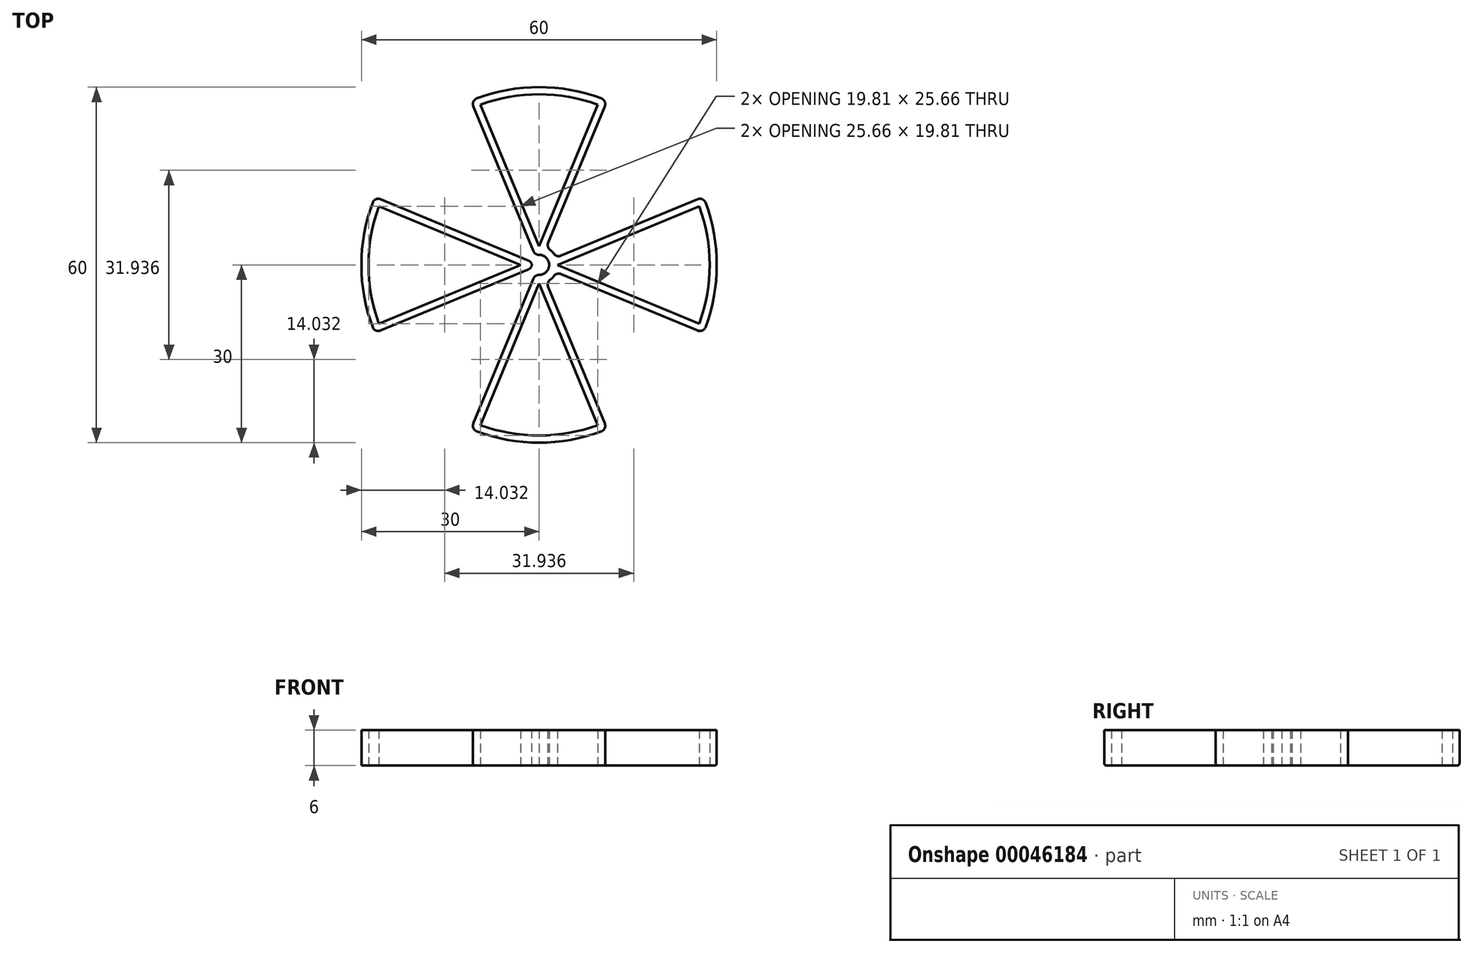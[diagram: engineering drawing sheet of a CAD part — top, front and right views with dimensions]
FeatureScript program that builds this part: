
annotation { "Feature Type Name" : "Feature", "Feature Type Description" : "" }
export const myFeature = defineFeature(function(context is Context, id is Id, definition is map)
    precondition{}
    {
        {
            var Q0;
            Q0=qCreatedBy(makeId("Top.planeOp"),FACE);
            var sketch = newSketch(context, id + "F0", { "sketchPlane" : qUnion([Q0])});
            skArc(sketch, "E0", {"start": v(-1, -1.12) * mm, "mid": v(1.5, 0) * mm, "end": v(-1, 1.12) * mm, "construction": true});
            skLineSegment(sketch, "E1", {"start": v(-1, 1.12) * mm, "end": v(-1, -1.12) * mm, "construction": true});
            skArc(sketch, "E2.0", {"start": v(-1.2, -1.2) * mm, "mid": v(1.7, 0) * mm, "end": v(-1.2, 1.2) * mm});
            skLineSegment(sketch, "E2.1", {"start": v(-1.2, 1.2) * mm, "end": v(-1.2, -1.2) * mm});
            skCircle(sketch, "E3", {"center": v(0, 0) * mm, "radius": 30 * mm});
            skLineSegment(sketch, "E4", {"start": v(0, 0) * mm, "end": v(-21.21, 21.21) * mm, "construction": true});
            skLineSegment(sketch, "E5", {"start": v(0, 0) * mm, "end": v(-11.48, 27.72) * mm});
            skLineSegment(sketch, "E6.MirrorCS", {"start": v(0, 0) * mm, "end": v(11.48, 27.72) * mm});
            skCircle(sketch, "E7.0", {"center": v(0, 0) * mm, "radius": 28.8 * mm});
            skCircle(sketch, "E8", {"center": v(0, 0) * mm, "radius": 3.14 * mm});
            skLineSegment(sketch, "E9.MirrorCS", {"start": v(0, 0) * mm, "end": v(-27.72, 11.48) * mm});
            skLineSegment(sketch, "E10.MirrorCS", {"start": v(0, 0) * mm, "end": v(-27.72, -11.48) * mm});
            skLineSegment(sketch, "E11.MirrorCS", {"start": v(0, 0) * mm, "end": v(27.72, 11.48) * mm});
            skLineSegment(sketch, "E12.MirrorCS", {"start": v(0, 0) * mm, "end": v(27.72, -11.48) * mm});
            skLineSegment(sketch, "E13.MirrorCS", {"start": v(0, 0) * mm, "end": v(-11.48, -27.72) * mm});
            skLineSegment(sketch, "E14.MirrorCS", {"start": v(0, 0) * mm, "end": v(11.48, -27.72) * mm});
            skLineSegment(sketch, "E15.0", {"start": v(0, -3.14) * mm, "end": v(10.37, -28.18) * mm});
            skLineSegment(sketch, "E15.1", {"start": v(0, -3.14) * mm, "end": v(-10.37, -28.18) * mm});
            skLineSegment(sketch, "E16.0", {"start": v(3.14, 0) * mm, "end": v(28.18, -10.37) * mm});
            skLineSegment(sketch, "E16.1", {"start": v(3.14, 0) * mm, "end": v(28.18, 10.37) * mm});
            skLineSegment(sketch, "E17.0", {"start": v(0, 3.14) * mm, "end": v(10.37, 28.18) * mm});
            skLineSegment(sketch, "E17.1", {"start": v(0, 3.14) * mm, "end": v(-10.37, 28.18) * mm});
            skLineSegment(sketch, "E18.0", {"start": v(-3.14, 0) * mm, "end": v(-28.18, 10.37) * mm});
            skLineSegment(sketch, "E18.1", {"start": v(-3.14, 0) * mm, "end": v(-28.18, -10.37) * mm});
            skSolve(sketch);
        }
        {
            var Q0;
            {var subQ0=sQuery(id+"F0.wireOp",EDGE,"E5");var subQ1=sQuery(id+"F0.wireOp",EDGE,"E3");var subQ2=makeQuery(id+"F0.imprint","INTERSECT",VERTEX,{"derivedFrom":[subQ1,subQ0]});Q0=makeQuery(id+"F0.imprint","IMPRINT",FACE,{"disambiguationData":[TD([[makeQuery(id+"F0.imprint","IMPRINT",EDGE,{"disambiguationData":[TD([[subQ2,1.0]])],"derivedFrom":subQ1}),1.0]])]});}
            var Q1;
            {var subQ0=sQuery(id+"F0.wireOp",EDGE,"E8");var subQ1=sQuery(id+"F0.wireOp",EDGE,"E5");var subQ2=makeQuery(id+"F0.imprint","INTERSECT",VERTEX,{"derivedFrom":[subQ1,subQ0]});Q1=makeQuery(id+"F0.imprint","IMPRINT",FACE,{"disambiguationData":[TD([[makeQuery(id+"F0.imprint","IMPRINT",EDGE,{"disambiguationData":[TD([[subQ2,-1.0]])],"derivedFrom":subQ1}),-1.0]])]});}
            var Q2;
            {var subQ0=sQuery(id+"F0.wireOp",EDGE,"E6.MirrorCS");var subQ1=sQuery(id+"F0.wireOp",EDGE,"E3");var subQ2=makeQuery(id+"F0.imprint","INTERSECT",VERTEX,{"derivedFrom":[subQ1,subQ0]});Q2=makeQuery(id+"F0.imprint","IMPRINT",FACE,{"disambiguationData":[TD([[makeQuery(id+"F0.imprint","IMPRINT",EDGE,{"disambiguationData":[TD([[subQ2,-1.0]])],"derivedFrom":subQ1}),1.0]])]});}
            var Q3;
            {var subQ0=sQuery(id+"F0.wireOp",EDGE,"E8");var subQ1=sQuery(id+"F0.wireOp",EDGE,"E6.MirrorCS");var subQ2=makeQuery(id+"F0.imprint","INTERSECT",VERTEX,{"derivedFrom":[subQ1,subQ0]});Q3=makeQuery(id+"F0.imprint","IMPRINT",FACE,{"disambiguationData":[TD([[makeQuery(id+"F0.imprint","IMPRINT",EDGE,{"disambiguationData":[TD([[subQ2,-1.0]])],"derivedFrom":subQ1}),1.0]])]});}
            var Q4;
            {var subQ2=sQuery(id+"F0.wireOp",EDGE,"E6.MirrorCS");var subQ4=sQuery(id+"F0.wireOp",EDGE,"E2.0");var subQ5=makeQuery(id+"F0.imprint","INTERSECT",VERTEX,{"derivedFrom":[subQ4,subQ2]});Q4=makeQuery(id+"F0.imprint","IMPRINT",FACE,{"disambiguationData":[TD([[makeQuery(id+"F0.imprint","IMPRINT",EDGE,{"disambiguationData":[TD([[subQ5,-1.0]])],"derivedFrom":subQ4}),-1.0]])]});}
            var Q5;
            {var subQ5=sQuery(id+"F0.wireOp",EDGE,"E2.0");var subQ7=sQuery(id+"F0.wireOp",EDGE,"E2.1");var subQ8=makeQuery(id+"F0.imprint","INTERSECT",VERTEX,{"disambiguationData":[OD(1.0)],"derivedFrom":[subQ5,subQ7]});Q5=makeQuery(id+"F0.imprint","IMPRINT",FACE,{"disambiguationData":[TD([[makeQuery(id+"F0.imprint","IMPRINT",EDGE,{"disambiguationData":[TD([[subQ8,1.0]])],"derivedFrom":subQ5}),-1.0]])]});}
            var Q6;
            {var subQ0=sQuery(id+"F0.wireOp",EDGE,"E9.MirrorCS");var subQ1=sQuery(id+"F0.wireOp",EDGE,"E2.1");var subQ2=makeQuery(id+"F0.imprint","INTERSECT",VERTEX,{"derivedFrom":[subQ1,subQ0]});Q6=makeQuery(id+"F0.imprint","IMPRINT",FACE,{"disambiguationData":[TD([[makeQuery(id+"F0.imprint","IMPRINT",EDGE,{"disambiguationData":[TD([[subQ2,-1.0]])],"derivedFrom":subQ1}),-1.0]])]});}
            var Q7;
            {var subQ0=sQuery(id+"F0.wireOp",EDGE,"E9.MirrorCS");var subQ1=sQuery(id+"F0.wireOp",EDGE,"E7.0");var subQ2=makeQuery(id+"F0.imprint","INTERSECT",VERTEX,{"derivedFrom":[subQ1,subQ0]});Q7=makeQuery(id+"F0.imprint","IMPRINT",FACE,{"disambiguationData":[TD([[makeQuery(id+"F0.imprint","IMPRINT",EDGE,{"disambiguationData":[TD([[subQ2,-1.0]])],"derivedFrom":subQ1}),1.0]])]});}
            var Q8;
            {var subQ0=sQuery(id+"F0.wireOp",EDGE,"E9.MirrorCS");var subQ1=sQuery(id+"F0.wireOp",EDGE,"E3");var subQ2=makeQuery(id+"F0.imprint","INTERSECT",VERTEX,{"derivedFrom":[subQ1,subQ0]});Q8=makeQuery(id+"F0.imprint","IMPRINT",FACE,{"disambiguationData":[TD([[makeQuery(id+"F0.imprint","IMPRINT",EDGE,{"disambiguationData":[TD([[subQ2,-1.0]])],"derivedFrom":subQ1}),1.0]])]});}
            var Q9;
            {var subQ0=sQuery(id+"F0.wireOp",EDGE,"E10.MirrorCS");var subQ1=sQuery(id+"F0.wireOp",EDGE,"E3");var subQ2=makeQuery(id+"F0.imprint","INTERSECT",VERTEX,{"derivedFrom":[subQ1,subQ0]});Q9=makeQuery(id+"F0.imprint","IMPRINT",FACE,{"disambiguationData":[TD([[makeQuery(id+"F0.imprint","IMPRINT",EDGE,{"disambiguationData":[TD([[subQ2,1.0]])],"derivedFrom":subQ1}),1.0]])]});}
            var Q10;
            {var subQ0=sQuery(id+"F0.wireOp",EDGE,"E13.MirrorCS");var subQ1=sQuery(id+"F0.wireOp",EDGE,"E7.0");var subQ2=makeQuery(id+"F0.imprint","INTERSECT",VERTEX,{"derivedFrom":[subQ1,subQ0]});Q10=makeQuery(id+"F0.imprint","IMPRINT",FACE,{"disambiguationData":[TD([[makeQuery(id+"F0.imprint","IMPRINT",EDGE,{"disambiguationData":[TD([[subQ2,-1.0]])],"derivedFrom":subQ1}),1.0]])]});}
            var Q11;
            {var subQ0=sQuery(id+"F0.wireOp",EDGE,"E13.MirrorCS");var subQ1=sQuery(id+"F0.wireOp",EDGE,"E3");var subQ2=makeQuery(id+"F0.imprint","INTERSECT",VERTEX,{"derivedFrom":[subQ1,subQ0]});Q11=makeQuery(id+"F0.imprint","IMPRINT",FACE,{"disambiguationData":[TD([[makeQuery(id+"F0.imprint","IMPRINT",EDGE,{"disambiguationData":[TD([[subQ2,-1.0]])],"derivedFrom":subQ1}),1.0]])]});}
            var Q12;
            {var subQ0=sQuery(id+"F0.wireOp",EDGE,"E14.MirrorCS");var subQ1=sQuery(id+"F0.wireOp",EDGE,"E3");var subQ2=makeQuery(id+"F0.imprint","INTERSECT",VERTEX,{"derivedFrom":[subQ1,subQ0]});Q12=makeQuery(id+"F0.imprint","IMPRINT",FACE,{"disambiguationData":[TD([[makeQuery(id+"F0.imprint","IMPRINT",EDGE,{"disambiguationData":[TD([[subQ2,1.0]])],"derivedFrom":subQ1}),1.0]])]});}
            var Q13;
            {var subQ4=sQuery(id+"F0.wireOp",EDGE,"E13.MirrorCS");var subQ6=sQuery(id+"F0.wireOp",EDGE,"E2.0");var subQ7=makeQuery(id+"F0.imprint","INTERSECT",VERTEX,{"derivedFrom":[subQ6,subQ4]});Q13=makeQuery(id+"F0.imprint","IMPRINT",FACE,{"disambiguationData":[TD([[makeQuery(id+"F0.imprint","IMPRINT",EDGE,{"disambiguationData":[TD([[subQ7,-1.0]])],"derivedFrom":subQ6}),-1.0]])]});}
            var Q14;
            {var subQ0=sQuery(id+"F0.wireOp",EDGE,"E14.MirrorCS");var subQ1=sQuery(id+"F0.wireOp",EDGE,"E2.0");var subQ2=makeQuery(id+"F0.imprint","INTERSECT",VERTEX,{"derivedFrom":[subQ1,subQ0]});Q14=makeQuery(id+"F0.imprint","IMPRINT",FACE,{"disambiguationData":[TD([[makeQuery(id+"F0.imprint","IMPRINT",EDGE,{"disambiguationData":[TD([[subQ2,-1.0]])],"derivedFrom":subQ1}),-1.0]])]});}
            var Q15;
            {var subQ2=sQuery(id+"F0.wireOp",EDGE,"E12.MirrorCS");var subQ6=sQuery(id+"F0.wireOp",EDGE,"E2.0");var subQ7=makeQuery(id+"F0.imprint","INTERSECT",VERTEX,{"derivedFrom":[subQ6,subQ2]});Q15=makeQuery(id+"F0.imprint","IMPRINT",FACE,{"disambiguationData":[TD([[makeQuery(id+"F0.imprint","IMPRINT",EDGE,{"disambiguationData":[TD([[subQ7,-1.0]])],"derivedFrom":subQ6}),-1.0]])]});}
            var Q16;
            {var subQ0=sQuery(id+"F0.wireOp",EDGE,"E11.MirrorCS");var subQ1=sQuery(id+"F0.wireOp",EDGE,"E2.0");var subQ2=makeQuery(id+"F0.imprint","INTERSECT",VERTEX,{"derivedFrom":[subQ1,subQ0]});Q16=makeQuery(id+"F0.imprint","IMPRINT",FACE,{"disambiguationData":[TD([[makeQuery(id+"F0.imprint","IMPRINT",EDGE,{"disambiguationData":[TD([[subQ2,-1.0]])],"derivedFrom":subQ1}),-1.0]])]});}
            var Q17;
            {var subQ0=sQuery(id+"F0.wireOp",EDGE,"E11.MirrorCS");var subQ1=sQuery(id+"F0.wireOp",EDGE,"E7.0");var subQ2=makeQuery(id+"F0.imprint","INTERSECT",VERTEX,{"derivedFrom":[subQ1,subQ0]});Q17=makeQuery(id+"F0.imprint","IMPRINT",FACE,{"disambiguationData":[TD([[makeQuery(id+"F0.imprint","IMPRINT",EDGE,{"disambiguationData":[TD([[subQ2,1.0]])],"derivedFrom":subQ1}),1.0]])]});}
            var Q18;
            {var subQ0=sQuery(id+"F0.wireOp",EDGE,"E11.MirrorCS");var subQ1=sQuery(id+"F0.wireOp",EDGE,"E3");var subQ2=makeQuery(id+"F0.imprint","INTERSECT",VERTEX,{"derivedFrom":[subQ1,subQ0]});Q18=makeQuery(id+"F0.imprint","IMPRINT",FACE,{"disambiguationData":[TD([[makeQuery(id+"F0.imprint","IMPRINT",EDGE,{"disambiguationData":[TD([[subQ2,1.0]])],"derivedFrom":subQ1}),1.0]])]});}
            var Q19;
            {var subQ0=sQuery(id+"F0.wireOp",EDGE,"E12.MirrorCS");var subQ1=sQuery(id+"F0.wireOp",EDGE,"E7.0");var subQ2=makeQuery(id+"F0.imprint","INTERSECT",VERTEX,{"derivedFrom":[subQ1,subQ0]});Q19=makeQuery(id+"F0.imprint","IMPRINT",FACE,{"disambiguationData":[TD([[makeQuery(id+"F0.imprint","IMPRINT",EDGE,{"disambiguationData":[TD([[subQ2,-1.0]])],"derivedFrom":subQ1}),1.0]])]});}
            var Q20;
            {var subQ0=sQuery(id+"F0.wireOp",EDGE,"E12.MirrorCS");var subQ1=sQuery(id+"F0.wireOp",EDGE,"E3");var subQ2=makeQuery(id+"F0.imprint","INTERSECT",VERTEX,{"derivedFrom":[subQ1,subQ0]});Q20=makeQuery(id+"F0.imprint","IMPRINT",FACE,{"disambiguationData":[TD([[makeQuery(id+"F0.imprint","IMPRINT",EDGE,{"disambiguationData":[TD([[subQ2,-1.0]])],"derivedFrom":subQ1}),1.0]])]});}
            var Q21;
            {var subQ5=sQuery(id+"F0.wireOp",EDGE,"E2.1");var subQ6=sQuery(id+"F0.wireOp",EDGE,"E2.0");var subQ7=makeQuery(id+"F0.imprint","INTERSECT",VERTEX,{"disambiguationData":[OD(0.0)],"derivedFrom":[subQ6,subQ5]});Q21=makeQuery(id+"F0.imprint","IMPRINT",FACE,{"disambiguationData":[TD([[makeQuery(id+"F0.imprint","IMPRINT",EDGE,{"disambiguationData":[TD([[subQ7,-1.0]])],"derivedFrom":subQ6}),-1.0]])]});}
            var Q22;
            {var subQ0=sQuery(id+"F0.wireOp",EDGE,"E15.0");var subQ1=sQuery(id+"F0.wireOp",EDGE,"E7.0");var subQ2=makeQuery(id+"F0.imprint","INTERSECT",VERTEX,{"derivedFrom":[subQ1,subQ0]});Q22=makeQuery(id+"F0.imprint","IMPRINT",FACE,{"disambiguationData":[TD([[makeQuery(id+"F0.imprint","IMPRINT",EDGE,{"disambiguationData":[TD([[subQ2,-1.0]])],"derivedFrom":subQ1}),1.0]])]});}
            var Q23;
            {var subQ0=sQuery(id+"F0.wireOp",EDGE,"E18.1");var subQ1=sQuery(id+"F0.wireOp",EDGE,"E7.0");var subQ2=makeQuery(id+"F0.imprint","INTERSECT",VERTEX,{"derivedFrom":[subQ1,subQ0]});Q23=makeQuery(id+"F0.imprint","IMPRINT",FACE,{"disambiguationData":[TD([[makeQuery(id+"F0.imprint","IMPRINT",EDGE,{"disambiguationData":[TD([[subQ2,-1.0]])],"derivedFrom":subQ1}),1.0]])]});}
            var Q24;
            {var subQ0=sQuery(id+"F0.wireOp",EDGE,"E11.MirrorCS");var subQ1=sQuery(id+"F0.wireOp",EDGE,"E3");var subQ2=makeQuery(id+"F0.imprint","INTERSECT",VERTEX,{"derivedFrom":[subQ1,subQ0]});Q24=makeQuery(id+"F0.imprint","IMPRINT",FACE,{"disambiguationData":[TD([[makeQuery(id+"F0.imprint","IMPRINT",EDGE,{"disambiguationData":[TD([[subQ2,1.0]])],"derivedFrom":subQ1}),1.0]])]});}
            var Q25;
            {var subQ0=sQuery(id+"F0.wireOp",EDGE,"E6.MirrorCS");var subQ1=sQuery(id+"F0.wireOp",EDGE,"E3");var subQ2=makeQuery(id+"F0.imprint","INTERSECT",VERTEX,{"derivedFrom":[subQ1,subQ0]});Q25=makeQuery(id+"F0.imprint","IMPRINT",FACE,{"disambiguationData":[TD([[makeQuery(id+"F0.imprint","IMPRINT",EDGE,{"disambiguationData":[TD([[subQ2,-1.0]])],"derivedFrom":subQ1}),1.0]])]});}
            var Q26;
            {var subQ0=sQuery(id+"F0.wireOp",EDGE,"E17.0");var subQ1=sQuery(id+"F0.wireOp",EDGE,"E3");var subQ2=makeQuery(id+"F0.imprint","INTERSECT",VERTEX,{"derivedFrom":[subQ1,subQ0]});Q26=makeQuery(id+"F0.imprint","IMPRINT",FACE,{"disambiguationData":[TD([[makeQuery(id+"F0.imprint","IMPRINT",EDGE,{"disambiguationData":[TD([[subQ2,-1.0]])],"derivedFrom":subQ1}),1.0]])]});}
            var Q27;
            {var subQ0=sQuery(id+"F0.wireOp",EDGE,"E5");var subQ1=sQuery(id+"F0.wireOp",EDGE,"E3");var subQ2=makeQuery(id+"F0.imprint","INTERSECT",VERTEX,{"derivedFrom":[subQ1,subQ0]});Q27=makeQuery(id+"F0.imprint","IMPRINT",FACE,{"disambiguationData":[TD([[makeQuery(id+"F0.imprint","IMPRINT",EDGE,{"disambiguationData":[TD([[subQ2,1.0]])],"derivedFrom":subQ1}),1.0]])]});}
            var Q28;
            {var subQ0=sQuery(id+"F0.wireOp",EDGE,"E9.MirrorCS");var subQ1=sQuery(id+"F0.wireOp",EDGE,"E3");var subQ2=makeQuery(id+"F0.imprint","INTERSECT",VERTEX,{"derivedFrom":[subQ1,subQ0]});Q28=makeQuery(id+"F0.imprint","IMPRINT",FACE,{"disambiguationData":[TD([[makeQuery(id+"F0.imprint","IMPRINT",EDGE,{"disambiguationData":[TD([[subQ2,-1.0]])],"derivedFrom":subQ1}),1.0]])]});}
            var Q29;
            {var subQ0=sQuery(id+"F0.wireOp",EDGE,"E18.0");var subQ1=sQuery(id+"F0.wireOp",EDGE,"E3");var subQ2=makeQuery(id+"F0.imprint","INTERSECT",VERTEX,{"derivedFrom":[subQ1,subQ0]});Q29=makeQuery(id+"F0.imprint","IMPRINT",FACE,{"disambiguationData":[TD([[makeQuery(id+"F0.imprint","IMPRINT",EDGE,{"disambiguationData":[TD([[subQ2,-1.0]])],"derivedFrom":subQ1}),1.0]])]});}
            var Q30;
            {var subQ0=sQuery(id+"F0.wireOp",EDGE,"E10.MirrorCS");var subQ1=sQuery(id+"F0.wireOp",EDGE,"E3");var subQ2=makeQuery(id+"F0.imprint","INTERSECT",VERTEX,{"derivedFrom":[subQ1,subQ0]});Q30=makeQuery(id+"F0.imprint","IMPRINT",FACE,{"disambiguationData":[TD([[makeQuery(id+"F0.imprint","IMPRINT",EDGE,{"disambiguationData":[TD([[subQ2,1.0]])],"derivedFrom":subQ1}),1.0]])]});}
            var Q31;
            {var subQ0=sQuery(id+"F0.wireOp",EDGE,"E13.MirrorCS");var subQ1=sQuery(id+"F0.wireOp",EDGE,"E3");var subQ2=makeQuery(id+"F0.imprint","INTERSECT",VERTEX,{"derivedFrom":[subQ1,subQ0]});Q31=makeQuery(id+"F0.imprint","IMPRINT",FACE,{"disambiguationData":[TD([[makeQuery(id+"F0.imprint","IMPRINT",EDGE,{"disambiguationData":[TD([[subQ2,-1.0]])],"derivedFrom":subQ1}),1.0]])]});}
            var Q32;
            {var subQ0=sQuery(id+"F0.wireOp",EDGE,"E15.1");var subQ1=sQuery(id+"F0.wireOp",EDGE,"E3");var subQ2=makeQuery(id+"F0.imprint","INTERSECT",VERTEX,{"derivedFrom":[subQ1,subQ0]});Q32=makeQuery(id+"F0.imprint","IMPRINT",FACE,{"disambiguationData":[TD([[makeQuery(id+"F0.imprint","IMPRINT",EDGE,{"disambiguationData":[TD([[subQ2,-1.0]])],"derivedFrom":subQ1}),1.0]])]});}
            var Q33;
            {var subQ0=sQuery(id+"F0.wireOp",EDGE,"E14.MirrorCS");var subQ1=sQuery(id+"F0.wireOp",EDGE,"E3");var subQ2=makeQuery(id+"F0.imprint","INTERSECT",VERTEX,{"derivedFrom":[subQ1,subQ0]});Q33=makeQuery(id+"F0.imprint","IMPRINT",FACE,{"disambiguationData":[TD([[makeQuery(id+"F0.imprint","IMPRINT",EDGE,{"disambiguationData":[TD([[subQ2,1.0]])],"derivedFrom":subQ1}),1.0]])]});}
            var Q34;
            {var subQ0=sQuery(id+"F0.wireOp",EDGE,"E12.MirrorCS");var subQ1=sQuery(id+"F0.wireOp",EDGE,"E3");var subQ2=makeQuery(id+"F0.imprint","INTERSECT",VERTEX,{"derivedFrom":[subQ1,subQ0]});Q34=makeQuery(id+"F0.imprint","IMPRINT",FACE,{"disambiguationData":[TD([[makeQuery(id+"F0.imprint","IMPRINT",EDGE,{"disambiguationData":[TD([[subQ2,-1.0]])],"derivedFrom":subQ1}),1.0]])]});}
            var Q35;
            {var subQ0=sQuery(id+"F0.wireOp",EDGE,"E16.1");var subQ1=sQuery(id+"F0.wireOp",EDGE,"E3");var subQ2=makeQuery(id+"F0.imprint","INTERSECT",VERTEX,{"derivedFrom":[subQ1,subQ0]});Q35=makeQuery(id+"F0.imprint","IMPRINT",FACE,{"disambiguationData":[TD([[makeQuery(id+"F0.imprint","IMPRINT",EDGE,{"disambiguationData":[TD([[subQ2,1.0]])],"derivedFrom":subQ1}),1.0]])]});}
            extrude(context, id + "F1", {"entities" : qUnion([Q0, Q1, Q2, Q3, Q4, Q5, Q6, Q7, Q8, Q9, Q10, Q11, Q12, Q13, Q14, Q15, Q16, Q17, Q18, Q19, Q20, Q21, Q22, Q23, Q24, Q25, Q26, Q27, Q28, Q29, Q30, Q31, Q32, Q33, Q34, Q35]), "depth" : 6 * mm, "offsetDistance" : 25 * mm});
        }
        {
            var Q0;
            Q0=makeQuery(id+"F1.opExtrude","SWEPT_EDGE",EDGE,{"disambiguationData":[OSD([sQuery(id+"F0.wireOp",EDGE,"E3"),sQuery(id+"F0.wireOp",EDGE,"E5")])]});
            var Q1;
            Q1=makeQuery(id+"F1.opExtrude","SWEPT_EDGE",EDGE,{"disambiguationData":[OSD([sQuery(id+"F0.wireOp",EDGE,"E3"),sQuery(id+"F0.wireOp",EDGE,"E6.MirrorCS")])]});
            var Q2;
            Q2=makeQuery(id+"F1.opExtrude","SWEPT_EDGE",EDGE,{"disambiguationData":[OSD([sQuery(id+"F0.wireOp",EDGE,"E3"),sQuery(id+"F0.wireOp",EDGE,"E9.MirrorCS")])]});
            var Q3;
            Q3=makeQuery(id+"F1.opExtrude","SWEPT_EDGE",EDGE,{"disambiguationData":[OSD([sQuery(id+"F0.wireOp",EDGE,"E5"),sQuery(id+"F0.wireOp",EDGE,"E8")])]});
            var Q4;
            Q4=makeQuery(id+"F1.opExtrude","SWEPT_EDGE",EDGE,{"disambiguationData":[OSD([sQuery(id+"F0.wireOp",EDGE,"E8"),sQuery(id+"F0.wireOp",EDGE,"E9.MirrorCS")])]});
            var Q5;
            Q5=makeQuery(id+"F1.opExtrude","SWEPT_EDGE",EDGE,{"disambiguationData":[OSD([sQuery(id+"F0.wireOp",EDGE,"E3"),sQuery(id+"F0.wireOp",EDGE,"E10.MirrorCS")])]});
            var Q6;
            Q6=makeQuery(id+"F1.opExtrude","SWEPT_EDGE",EDGE,{"disambiguationData":[OSD([sQuery(id+"F0.wireOp",EDGE,"E3"),sQuery(id+"F0.wireOp",EDGE,"E13.MirrorCS")])]});
            var Q7;
            Q7=makeQuery(id+"F1.opExtrude","SWEPT_EDGE",EDGE,{"disambiguationData":[OSD([sQuery(id+"F0.wireOp",EDGE,"E3"),sQuery(id+"F0.wireOp",EDGE,"E11.MirrorCS")])]});
            var Q8;
            Q8=makeQuery(id+"F1.opExtrude","SWEPT_EDGE",EDGE,{"disambiguationData":[OSD([sQuery(id+"F0.wireOp",EDGE,"E8"),sQuery(id+"F0.wireOp",EDGE,"E10.MirrorCS")])]});
            var Q9;
            Q9=makeQuery(id+"F1.opExtrude","SWEPT_EDGE",EDGE,{"disambiguationData":[OSD([sQuery(id+"F0.wireOp",EDGE,"E8"),sQuery(id+"F0.wireOp",EDGE,"E13.MirrorCS")])]});
            var Q10;
            Q10=makeQuery(id+"F1.opExtrude","SWEPT_EDGE",EDGE,{"disambiguationData":[OSD([sQuery(id+"F0.wireOp",EDGE,"E8"),sQuery(id+"F0.wireOp",EDGE,"E14.MirrorCS")])]});
            var Q11;
            Q11=makeQuery(id+"F1.opExtrude","SWEPT_EDGE",EDGE,{"disambiguationData":[OSD([sQuery(id+"F0.wireOp",EDGE,"E8"),sQuery(id+"F0.wireOp",EDGE,"E12.MirrorCS")])]});
            var Q12;
            Q12=makeQuery(id+"F1.opExtrude","SWEPT_EDGE",EDGE,{"disambiguationData":[OSD([sQuery(id+"F0.wireOp",EDGE,"E3"),sQuery(id+"F0.wireOp",EDGE,"E14.MirrorCS")])]});
            var Q13;
            Q13=makeQuery(id+"F1.opExtrude","SWEPT_EDGE",EDGE,{"disambiguationData":[OSD([sQuery(id+"F0.wireOp",EDGE,"E3"),sQuery(id+"F0.wireOp",EDGE,"E12.MirrorCS")])]});
            var Q14;
            Q14=makeQuery(id+"F1.opExtrude","SWEPT_EDGE",EDGE,{"disambiguationData":[OSD([sQuery(id+"F0.wireOp",EDGE,"E6.MirrorCS"),sQuery(id+"F0.wireOp",EDGE,"E8")])]});
            var Q15;
            Q15=makeQuery(id+"F1.opExtrude","SWEPT_EDGE",EDGE,{"disambiguationData":[OSD([sQuery(id+"F0.wireOp",EDGE,"E8"),sQuery(id+"F0.wireOp",EDGE,"E11.MirrorCS")])]});
            fillet(context, id + "F2", {"entities" : qUnion([Q0, Q1, Q2, Q3, Q4, Q5, Q6, Q7, Q8, Q9, Q10, Q11, Q12, Q13, Q14, Q15]), "tangentPropagation" : true, "radius" : 1 * mm, "defaultsChanged" : false, "vertexSettings" : [], "allowEdgeOverflow" : false});
        }
        {
            var Q0;
            Q0=makeQuery(id+"F1.opExtrude","CAP_EDGE",EDGE,{"disambiguationData":[OSD([sQuery(id+"F0.wireOp",EDGE,"E2.1")])],"isStart":true});
            var Q1;
            Q1=makeQuery(id+"F1.opExtrude","CAP_EDGE",EDGE,{"disambiguationData":[OSD([sQuery(id+"F0.wireOp",EDGE,"E2.0")])],"isStart":true});
            var Q2;
            {var subQ0=sQuery(id+"F0.wireOp",EDGE,"E10.MirrorCS");var subQ1=sQuery(id+"F0.wireOp",EDGE,"E8");Q2=makeQuery(id+"F2.opFillet","BLEND_EDGE",EDGE,{"blendedFrom":[makeQuery(id+"F1.opExtrude","SWEPT_EDGE",EDGE,{"disambiguationData":[OSD([subQ1,subQ0])]}),makeQuery(id+"F1.opExtrude","CAP_FACE",FACE,{"disambiguationData":[OSD([sQuery(id+"F0.wireOp",EDGE,"E2.0"),sQuery(id+"F0.wireOp",EDGE,"E2.1"),sQuery(id+"F0.wireOp",EDGE,"E3"),sQuery(id+"F0.wireOp",EDGE,"E5"),sQuery(id+"F0.wireOp",EDGE,"E6.MirrorCS"),sQuery(id+"F0.wireOp",EDGE,"E7.0"),sQuery(id+"F0.wireOp",EDGE,"79e3b18a-ea47-41ee-b69a-72c01cc687a9.0"),sQuery(id+"F0.wireOp",EDGE,"79e3b18a-ea47-41ee-b69a-72c01cc687a9.1"),subQ1,sQuery(id+"F0.wireOp",EDGE,"E9.MirrorCS"),sQuery(id+"F0.wireOp",EDGE,"a22ce600-2d97-45e9-b27f-ca5ae6c290080.MirrorCS"),sQuery(id+"F0.wireOp",EDGE,"c8a25dc1-bed8-48e5-9f05-997fd0db33790.MirrorCS"),subQ0,sQuery(id+"F0.wireOp",EDGE,"E11.MirrorCS"),sQuery(id+"F0.wireOp",EDGE,"1493616c-501a-4236-988d-a5bc47dabbc30.MirrorCS"),sQuery(id+"F0.wireOp",EDGE,"118f354a-c613-46d3-8d89-93113810e2ad0.MirrorCS"),sQuery(id+"F0.wireOp",EDGE,"E12.MirrorCS"),sQuery(id+"F0.wireOp",EDGE,"E13.MirrorCS"),sQuery(id+"F0.wireOp",EDGE,"8d252170-ec07-4a0a-b810-06c3c216fb470.MirrorCS"),sQuery(id+"F0.wireOp",EDGE,"6849afd2-6876-4460-b7e8-ec682c4397300.MirrorCS"),sQuery(id+"F0.wireOp",EDGE,"E14.MirrorCS")])],"isStart":true})],"blendedInto":[makeQuery(id+"F1.opExtrude","CAP_FACE",FACE,{"disambiguationData":[OSD([sQuery(id+"F0.wireOp",EDGE,"E2.0"),sQuery(id+"F0.wireOp",EDGE,"E2.1"),sQuery(id+"F0.wireOp",EDGE,"E3"),sQuery(id+"F0.wireOp",EDGE,"E5"),sQuery(id+"F0.wireOp",EDGE,"E6.MirrorCS"),sQuery(id+"F0.wireOp",EDGE,"E7.0"),sQuery(id+"F0.wireOp",EDGE,"79e3b18a-ea47-41ee-b69a-72c01cc687a9.0"),sQuery(id+"F0.wireOp",EDGE,"79e3b18a-ea47-41ee-b69a-72c01cc687a9.1"),subQ1,sQuery(id+"F0.wireOp",EDGE,"E9.MirrorCS"),sQuery(id+"F0.wireOp",EDGE,"a22ce600-2d97-45e9-b27f-ca5ae6c290080.MirrorCS"),sQuery(id+"F0.wireOp",EDGE,"c8a25dc1-bed8-48e5-9f05-997fd0db33790.MirrorCS"),subQ0,sQuery(id+"F0.wireOp",EDGE,"E11.MirrorCS"),sQuery(id+"F0.wireOp",EDGE,"1493616c-501a-4236-988d-a5bc47dabbc30.MirrorCS"),sQuery(id+"F0.wireOp",EDGE,"118f354a-c613-46d3-8d89-93113810e2ad0.MirrorCS"),sQuery(id+"F0.wireOp",EDGE,"E12.MirrorCS"),sQuery(id+"F0.wireOp",EDGE,"E13.MirrorCS"),sQuery(id+"F0.wireOp",EDGE,"8d252170-ec07-4a0a-b810-06c3c216fb470.MirrorCS"),sQuery(id+"F0.wireOp",EDGE,"6849afd2-6876-4460-b7e8-ec682c4397300.MirrorCS"),sQuery(id+"F0.wireOp",EDGE,"E14.MirrorCS")])],"isStart":true})]});}
            fillet(context, id + "F3", {"entities" : qUnion([Q0, Q1, Q2]), "tangentPropagation" : true, "radius" : .4 * mm, "defaultsChanged" : false, "vertexSettings" : [], "allowEdgeOverflow" : false});
        }
    });
